# Revit family: 3039986 Lighting Fixture_Sylvania_Lumina Edge LED_Wall Mounted
name_source: partatom
category: Lighting Fixtures
revit_build: Autodesk Revit 2017 (Build: 20190507_1515(x64)
units: mm (PartAtom-declared; Revit-internal decimal feet)

## family parameters
Cut with Voids When Loaded = No
Host = Face
Light Source = Yes
OmniClass Number = 23.80.70.11.17
OmniClass Title = Specialized Lighting by Location or Use
Part Type = Normal
Room Calculation Point = No
Round Connector Dimension = Use Diameter
Shared = No

## types (1)
- Lumina Edge LED 2700K
    Apparent Load = 12 VA
    Assembly Code = D5020200
    Body Material = Aluminum_Sylvania_Edge LED_White_RAL 9016
    Color Filter = 16777215
    Default Elevation = 0 mm  [stored 0 ft]
    Description = Lumina LED is a new range of ambient & decorative LED wall lights. Consisting of multiple decorative styles, they are suitable for use in any hospitality or residential application such as reception areas, hallways and lounge spaces. Lumina LED offers a selection of different styles to suit multiple applications. With a 2,700K colour temperature it provides a soft and ambient lighting effect. Lumina LED provides direct/indirect ambient light with an efficacy of up to 87lm/W; up to 50% more energy efficient than equivalent products using traditional lamp sources.
    Diffuser Length = 310 mm  [stored 1.01706 ft]
    Diffuser Material = Polycarbonate_Sylvania_Edge LED_Clear
    Dimming Lamp Color Temperature Shift = <None>
    Drive Current = 350mA
    Electrical Protection = Class II
    Emit Shape Visible in Rendering = No
    Emit from Rectangle Length = 310 mm  [stored 1.01706 ft]
    Emit from Rectangle Width = 25 mm  [stored 0.082021 ft]
    Energy Class = A++, A+, A
    Height = 55 mm  [stored 0.180446 ft]
    IP Rating = IP20
    Lamp = LED
    Length = 330 mm  [stored 1.08268 ft]
    Life = 30 000h
    Light Distribution = Indirect
    Manufacturer = Feilo Sylvania
    Model = 3039986 Lumina Edge LED 2700K
    Mounting Length = 100 mm  [stored 0.328084 ft]
    Photometric Web File = 3039986_LuminaEdgeLED2700K-183080.ies
    Product Family = Lumina LED
    Product Page URL = http://www.sylvania-lighting.com
    Tilt Angle = -90.00°
    URL = http://www.sylvania-lighting.com
    Voltage = 240 V
    Voltage Comments = UNV (Universal Voltage; 100-240 Volt)
    Width = 78 mm  [stored 0.255906 ft]

note: [stored X ft] marks values corroborated as IEEE doubles in the binary element streams (Revit-internal decimal feet)

## geometry (parser evidence)
native form markers: Blend x4, Sweep x2
no freeform markers — native parametric forms only
